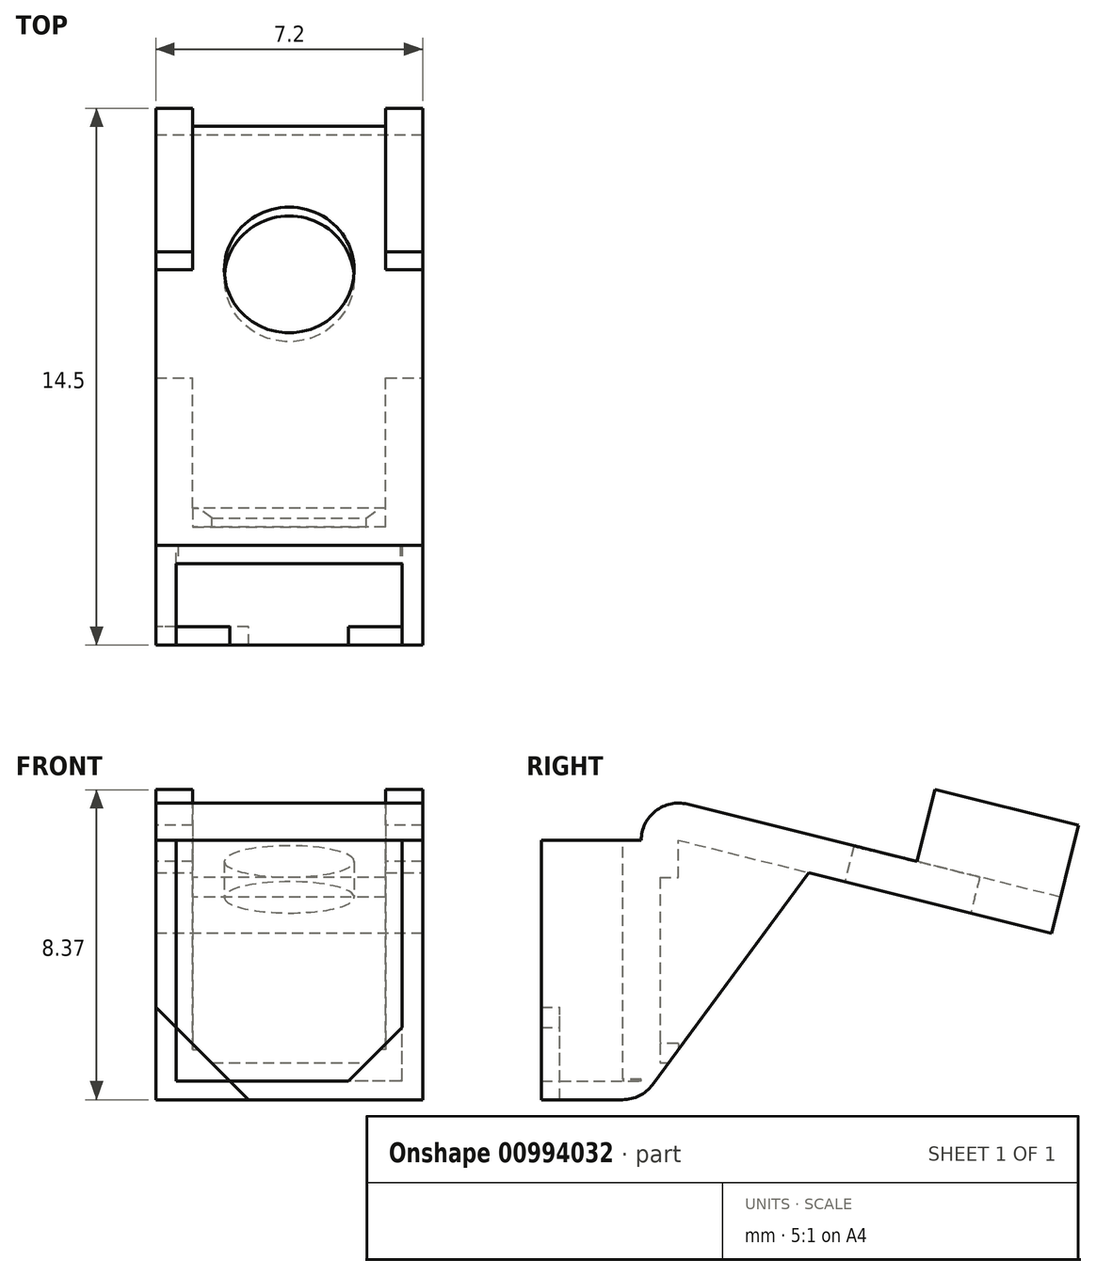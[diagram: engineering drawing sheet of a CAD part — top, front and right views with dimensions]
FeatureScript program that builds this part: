
annotation { "Feature Type Name" : "Feature", "Feature Type Description" : "" }
export const myFeature = defineFeature(function(context is Context, id is Id, definition is map)
    precondition{}
    {
        {
            var Q0;
            Q0=qCreatedBy(makeId("Front.planeOp"),FACE);
            var sketch = newSketch(context, id + "F0", { "sketchPlane" : qUnion([Q0])});
            skLineSegment(sketch, "E0.bottom", {"start": v(3.6, -3.5) * mm, "end": v(-3.6, -3.5) * mm});
            skLineSegment(sketch, "E0.top", {"start": v(3.6, 3.5) * mm, "end": v(-3.6, 3.5) * mm});
            skLineSegment(sketch, "E0.left", {"start": v(3.6, -3.5) * mm, "end": v(3.6, 3.5) * mm});
            skLineSegment(sketch, "E0.right", {"start": v(-3.6, -3.5) * mm, "end": v(-3.6, 3.5) * mm});
            skPoint(sketch, "E0.middle", {"position": v(0, 0) * mm});
            skLineSegment(sketch, "E1.bottom", {"start": v(3.05, -3) * mm, "end": v(-3.05, -3) * mm});
            skLineSegment(sketch, "E1.top", {"start": v(3.05, 3) * mm, "end": v(-3.05, 3) * mm});
            skLineSegment(sketch, "E1.left", {"start": v(3.05, -3) * mm, "end": v(3.05, 3) * mm});
            skLineSegment(sketch, "E1.right", {"start": v(-3.05, -3) * mm, "end": v(-3.05, 3) * mm});
            skLineSegment(sketch, "E2", {"start": v(-3.6, 3.5) * mm, "end": v(-3.6, 2.4) * mm});
            skLineSegment(sketch, "E3", {"start": v(-3.6, 3.5) * mm, "end": v(-2.5, 3.5) * mm});
            skLineSegment(sketch, "E4.MirrorCS", {"start": v(3.6, 3.5) * mm, "end": v(2.5, 3.5) * mm});
            skLineSegment(sketch, "E5.MirrorCS", {"start": v(3.6, 3.5) * mm, "end": v(3.6, 2.4) * mm});
            skLineSegment(sketch, "E6.MirrorCS", {"start": v(-3.6, -3.5) * mm, "end": v(-3.6, -2.4) * mm});
            skLineSegment(sketch, "E7.MirrorCS", {"start": v(-3.6, -3.5) * mm, "end": v(-2.5, -3.5) * mm});
            skLineSegment(sketch, "E8.MirrorCS", {"start": v(-3.05, -2.95) * mm, "end": v(-3, -3) * mm});
            skLineSegment(sketch, "E9.MirrorCS", {"start": v(3.6, -3.5) * mm, "end": v(2.5, -3.5) * mm});
            skLineSegment(sketch, "E10.MirrorCS", {"start": v(3.6, -3.5) * mm, "end": v(3.6, -2.4) * mm});
            skLineSegment(sketch, "E11.MirrorCS", {"start": v(3.05, -2.95) * mm, "end": v(3, -3) * mm});
            skPoint(sketch, "E12.orphan", {"position": v(-3.6, -2.4) * mm});
            skPoint(sketch, "E13.orphan", {"position": v(-2.5, -3.5) * mm});
            skPoint(sketch, "E14.orphan", {"position": v(2.5, -3.5) * mm});
            skPoint(sketch, "E15.orphan", {"position": v(3.6, -2.4) * mm});
            skPoint(sketch, "E16.orphan", {"position": v(2.5, 3.5) * mm});
            skPoint(sketch, "E17.orphan", {"position": v(3.6, 2.4) * mm});
            skLineSegment(sketch, "E18", {"start": v(-3.05, -3) * mm, "end": v(-3.05, -3.5) * mm});
            skLineSegment(sketch, "E19", {"start": v(3.05, -3) * mm, "end": v(3.05, -3.5) * mm});
            skLineSegment(sketch, "E20.MirrorCS", {"start": v(-3.05, 3) * mm, "end": v(-3.05, 3.5) * mm});
            skLineSegment(sketch, "E21.MirrorCS", {"start": v(3.05, 3) * mm, "end": v(3.05, 3.5) * mm});
            skSolve(sketch);
        }
        {
            var Q0;
            Q0=makeQuery(id+"F0.imprint","IMPRINT",FACE,{"disambiguationData":[TD([[makeQuery(id+"F0.imprint","IMPRINT",EDGE,{"derivedFrom":sQuery(id+"F0.wireOp",EDGE,"E0.right")}),-1.0]])]});
            var Q1;
            {var subQ5=sQuery(id+"F0.wireOp",EDGE,"E0.bottom");Q1=makeQuery(id+"F0.imprint","IMPRINT",FACE,{"disambiguationData":[TD([[makeQuery(id+"F0.imprint","IMPRINT",EDGE,{"derivedFrom":subQ5}),-1.0]])]});}
            var Q2;
            Q2=makeQuery(id+"F0.imprint","IMPRINT",FACE,{"disambiguationData":[TD([[makeQuery(id+"F0.imprint","IMPRINT",EDGE,{"derivedFrom":sQuery(id+"F0.wireOp",EDGE,"E0.left")}),1.0]])]});
            extrude(context, id + "F1", {"entities" : qUnion([Q0, Q1, Q2]), "depth" : 1.7 * mm, "offsetDistance" : 25 * mm});
        }
        {
            var Q0;
            Q0=makeQuery(id+"F0.imprint","IMPRINT",FACE,{"disambiguationData":[TD([[makeQuery(id+"F0.imprint","IMPRINT",EDGE,{"derivedFrom":sQuery(id+"F0.wireOp",EDGE,"E0.left")}),1.0]])]});
            var Q1;
            {var subQ5=sQuery(id+"F0.wireOp",EDGE,"E0.bottom");Q1=makeQuery(id+"F0.imprint","IMPRINT",FACE,{"disambiguationData":[TD([[makeQuery(id+"F0.imprint","IMPRINT",EDGE,{"derivedFrom":subQ5}),-1.0]])]});}
            var Q2;
            Q2=makeQuery(id+"F0.imprint","IMPRINT",FACE,{"disambiguationData":[TD([[makeQuery(id+"F0.imprint","IMPRINT",EDGE,{"derivedFrom":sQuery(id+"F0.wireOp",EDGE,"E0.right")}),-1.0]])]});
            var Q3;
            {var subQ1=sQuery(id+"F0.wireOp",EDGE,"E0.top");Q3=makeQuery(id+"F0.imprint","IMPRINT",FACE,{"disambiguationData":[TD([[makeQuery(id+"F0.imprint","IMPRINT",EDGE,{"derivedFrom":subQ1}),1.0]])]});}
            var Q4;
            {var subQ1=sQuery(id+"F0.wireOp",EDGE,"E1.top");Q4=makeQuery(id+"F0.imprint","IMPRINT",FACE,{"disambiguationData":[TD([[makeQuery(id+"F0.imprint","IMPRINT",EDGE,{"derivedFrom":subQ1}),1.0]])]});}
            extrude(context, id + "F2", {"entities" : qUnion([Q0, Q1, Q2, Q3, Q4]), "operationType" : NewBodyOperationType.ADD, "oppositeDirection" : true, "depth" : 0.5 * mm, "offsetDistance" : 25 * mm});
        }
        {
            var Q0;
            Q0=makeQuery(id+"F1.opExtrude","CAP_FACE",FACE,{"disambiguationData":[OSD([sQuery(id+"F0.wireOp",EDGE,"E0.bottom"),sQuery(id+"F0.wireOp",EDGE,"E0.top"),sQuery(id+"F0.wireOp",EDGE,"E0.left"),sQuery(id+"F0.wireOp",EDGE,"E0.right"),sQuery(id+"F0.wireOp",EDGE,"E1.bottom"),sQuery(id+"F0.wireOp",EDGE,"E1.top"),sQuery(id+"F0.wireOp",EDGE,"E1.left"),sQuery(id+"F0.wireOp",EDGE,"E1.right"),sQuery(id+"F0.wireOp",EDGE,"E2"),sQuery(id+"F0.wireOp",EDGE,"E3"),sQuery(id+"F0.wireOp",EDGE,"E4.MirrorCS"),sQuery(id+"F0.wireOp",EDGE,"E5.MirrorCS"),sQuery(id+"F0.wireOp",EDGE,"E6.MirrorCS"),sQuery(id+"F0.wireOp",EDGE,"E7.MirrorCS"),sQuery(id+"F0.wireOp",EDGE,"E9.MirrorCS"),sQuery(id+"F0.wireOp",EDGE,"E10.MirrorCS")])],"isStart":false});
            var sketch = newSketch(context, id + "F3", { "sketchPlane" : qUnion([Q0])});
            skLineSegment(sketch, "E22", {"start": v(-3.6, 3.5) * mm, "end": v(-1.1, 3.5) * mm});
            skLineSegment(sketch, "E23", {"start": v(-1.1, 3.5) * mm, "end": v(-3.6, 1) * mm});
            skLineSegment(sketch, "E24", {"start": v(-3.6, 1) * mm, "end": v(-3.6, 3.5) * mm});
            skLineSegment(sketch, "E25.MirrorCS", {"start": v(1.1, 3.5) * mm, "end": v(3.6, 1) * mm});
            skLineSegment(sketch, "E26.MirrorCS", {"start": v(3.6, 3.5) * mm, "end": v(1.1, 3.5) * mm});
            skLineSegment(sketch, "E27.MirrorCS", {"start": v(3.6, 1) * mm, "end": v(3.6, 3.5) * mm});
            skLineSegment(sketch, "E28.MirrorCS", {"start": v(-3.6, -3.5) * mm, "end": v(-1.1, -3.5) * mm});
            skLineSegment(sketch, "E29.MirrorCS", {"start": v(-3.6, -1) * mm, "end": v(-3.6, -3.5) * mm});
            skLineSegment(sketch, "E30.MirrorCS", {"start": v(-1.1, -3.5) * mm, "end": v(-3.6, -1) * mm});
            skLineSegment(sketch, "E31.MirrorCS", {"start": v(3.6, -3.5) * mm, "end": v(1.1, -3.5) * mm});
            skLineSegment(sketch, "E32.MirrorCS", {"start": v(3.6, -1) * mm, "end": v(3.6, -3.5) * mm});
            skLineSegment(sketch, "E33.MirrorCS", {"start": v(1.1, -3.5) * mm, "end": v(3.6, -1) * mm});
            skSolve(sketch);
        }
        {
            var Q0;
            {var subQ4=sQuery(id+"F3.wireOp",EDGE,"E22");Q0=makeQuery(id+"F3.imprint","IMPRINT",FACE,{"disambiguationData":[TD([[makeQuery(id+"F3.imprint","IMPRINT",EDGE,{"derivedFrom":subQ4}),1.0]])]});}
            var Q1;
            {var subQ0=sQuery(id+"F3.wireOp",EDGE,"E29.MirrorCS");Q1=makeQuery(id+"F3.imprint","IMPRINT",FACE,{"disambiguationData":[TD([[makeQuery(id+"F3.imprint","IMPRINT",EDGE,{"derivedFrom":subQ0}),1.0]])]});}
            var Q2;
            {var subQ0=sQuery(id+"F3.wireOp",EDGE,"E23");var subQ3=makeQuery(id+"F1.opExtrude","CAP_EDGE",EDGE,{"disambiguationData":[OSD([sQuery(id+"F0.wireOp",EDGE,"E1.top")])],"isStart":false});var subQ4=makeQuery(id+"F3.imprint","INTERSECT",VERTEX,{"derivedFrom":[subQ3,subQ0]});Q2=makeQuery(id+"F3.imprint","IMPRINT",FACE,{"disambiguationData":[TD([[makeQuery(id+"F3.imprint","IMPRINT",EDGE,{"disambiguationData":[TD([[subQ4,1.0]])],"derivedFrom":subQ3}),-1.0]])]});}
            var Q3;
            {var subQ0=sQuery(id+"F3.wireOp",EDGE,"E25.MirrorCS");var subQ3=makeQuery(id+"F1.opExtrude","CAP_EDGE",EDGE,{"disambiguationData":[OSD([sQuery(id+"F0.wireOp",EDGE,"E1.left"),sQuery(id+"F0.wireOp",EDGE,"E19")])],"isStart":false});var subQ4=makeQuery(id+"F3.imprint","INTERSECT",VERTEX,{"derivedFrom":[subQ3,subQ0]});Q3=makeQuery(id+"F3.imprint","IMPRINT",FACE,{"disambiguationData":[TD([[makeQuery(id+"F3.imprint","IMPRINT",EDGE,{"disambiguationData":[TD([[subQ4,1.0]])],"derivedFrom":subQ3}),-1.0]])]});}
            var Q4;
            {var subQ0=sQuery(id+"F3.wireOp",EDGE,"E32.MirrorCS");Q4=makeQuery(id+"F3.imprint","IMPRINT",FACE,{"disambiguationData":[TD([[makeQuery(id+"F3.imprint","IMPRINT",EDGE,{"derivedFrom":subQ0}),1.0]])]});}
            var Q5;
            {var subQ0=sQuery(id+"F3.wireOp",EDGE,"E24");Q5=makeQuery(id+"F3.imprint","IMPRINT",FACE,{"disambiguationData":[TD([[makeQuery(id+"F3.imprint","IMPRINT",EDGE,{"derivedFrom":subQ0}),1.0]])]});}
            var Q6;
            {var subQ0=sQuery(id+"F3.wireOp",EDGE,"E23");var subQ3=makeQuery(id+"F1.opExtrude","CAP_EDGE",EDGE,{"disambiguationData":[OSD([sQuery(id+"F0.wireOp",EDGE,"E1.right"),sQuery(id+"F0.wireOp",EDGE,"E20.MirrorCS")])],"isStart":false});var subQ4=makeQuery(id+"F3.imprint","INTERSECT",VERTEX,{"derivedFrom":[subQ3,subQ0]});Q6=makeQuery(id+"F3.imprint","IMPRINT",FACE,{"disambiguationData":[TD([[makeQuery(id+"F3.imprint","IMPRINT",EDGE,{"disambiguationData":[TD([[subQ4,1.0]])],"derivedFrom":subQ3}),1.0]])]});}
            var Q7;
            {var subQ0=sQuery(id+"F3.wireOp",EDGE,"E27.MirrorCS");Q7=makeQuery(id+"F3.imprint","IMPRINT",FACE,{"disambiguationData":[TD([[makeQuery(id+"F3.imprint","IMPRINT",EDGE,{"derivedFrom":subQ0}),1.0]])]});}
            var Q8;
            {var subQ0=sQuery(id+"F3.wireOp",EDGE,"E30.MirrorCS");var subQ3=makeQuery(id+"F1.opExtrude","CAP_EDGE",EDGE,{"disambiguationData":[OSD([sQuery(id+"F0.wireOp",EDGE,"E1.bottom")])],"isStart":false});var subQ4=makeQuery(id+"F3.imprint","INTERSECT",VERTEX,{"derivedFrom":[subQ3,subQ0]});Q8=makeQuery(id+"F3.imprint","IMPRINT",FACE,{"disambiguationData":[TD([[makeQuery(id+"F3.imprint","IMPRINT",EDGE,{"disambiguationData":[TD([[subQ4,1.0]])],"derivedFrom":subQ3}),1.0]])]});}
            var Q9;
            {var subQ0=sQuery(id+"F3.wireOp",EDGE,"E33.MirrorCS");var subQ1=makeQuery(id+"F1.opExtrude","CAP_EDGE",EDGE,{"disambiguationData":[OSD([sQuery(id+"F0.wireOp",EDGE,"E1.bottom")])],"isStart":false});var subQ2=makeQuery(id+"F3.imprint","INTERSECT",VERTEX,{"derivedFrom":[subQ1,subQ0]});Q9=makeQuery(id+"F3.imprint","IMPRINT",FACE,{"disambiguationData":[TD([[makeQuery(id+"F3.imprint","IMPRINT",EDGE,{"disambiguationData":[TD([[subQ2,-1.0]])],"derivedFrom":subQ0}),-1.0]])]});}
            var Q10;
            {var subQ0=sQuery(id+"F3.wireOp",EDGE,"E30.MirrorCS");var subQ1=makeQuery(id+"F1.opExtrude","CAP_EDGE",EDGE,{"disambiguationData":[OSD([sQuery(id+"F0.wireOp",EDGE,"E1.bottom")])],"isStart":false});var subQ2=makeQuery(id+"F3.imprint","INTERSECT",VERTEX,{"derivedFrom":[subQ1,subQ0]});Q10=makeQuery(id+"F3.imprint","IMPRINT",FACE,{"disambiguationData":[TD([[makeQuery(id+"F3.imprint","IMPRINT",EDGE,{"disambiguationData":[TD([[subQ2,-1.0]])],"derivedFrom":subQ0}),1.0]])]});}
            extrude(context, id + "F4", {"entities" : qUnion([Q0, Q1, Q2, Q3, Q4, Q5, Q6, Q7, Q8, Q9, Q10]), "operationType" : NewBodyOperationType.ADD, "depth" : 0.5 * mm, "offsetDistance" : 25 * mm});
        }
        {
            var Q0;
            {var subQ0=sQuery(id+"F0.wireOp",EDGE,"E10.MirrorCS");var subQ1=sQuery(id+"F0.wireOp",EDGE,"E5.MirrorCS");var subQ2=sQuery(id+"F0.wireOp",EDGE,"E0.left");Q0=makeQuery(id+"F4.boolean.opBoolean","MERGE",FACE,{"derivedFrom":[makeQuery(id+"F2.boolean.opBoolean","MERGE",FACE,{"derivedFrom":[makeQuery(id+"F1.opExtrude","SWEPT_FACE",FACE,{"disambiguationData":[OSD([subQ2,subQ1,subQ0])]}),makeQuery(id+"F2.opExtrude","SWEPT_FACE",FACE,{"disambiguationData":[OSD([subQ2,subQ1,subQ0])]})]}),makeQuery(id+"F4.opExtrude","SWEPT_FACE",FACE,{"disambiguationData":[OSD([subQ2,subQ1,subQ0,sQuery(id+"F3.wireOp",EDGE,"E27.MirrorCS"),sQuery(id+"F3.wireOp",EDGE,"E32.MirrorCS")])]})]});}
            var sketch = newSketch(context, id + "F5", { "sketchPlane" : qUnion([Q0])});
            skLineSegment(sketch, "E34", {"start": v(0.5, -3.5) * mm, "end": v(5.66, 3.5) * mm});
            skLineSegment(sketch, "E35", {"start": v(5.66, 3.5) * mm, "end": v(0.5, 3.5) * mm});
            skLineSegment(sketch, "E36", {"start": v(0.5, 3.5) * mm, "end": v(0.5, 4.79) * mm});
            skLineSegment(sketch, "E37", {"start": v(0.5, 4.79) * mm, "end": v(5.66, 3.5) * mm});
            skSolve(sketch);
        }
        {
            var Q0;
            Q0=makeQuery(id+"F5.imprint","IMPRINT",FACE,{"disambiguationData":[TD([[makeQuery(id+"F5.imprint","IMPRINT",EDGE,{"derivedFrom":sQuery(id+"F5.wireOp",EDGE,"E34")}),1.0]])]});
            var Q1;
            Q1=makeQuery(id+"F5.imprint","IMPRINT",FACE,{"disambiguationData":[TD([[makeQuery(id+"F5.imprint","IMPRINT",EDGE,{"derivedFrom":sQuery(id+"F5.wireOp",EDGE,"E35")}),-1.0]])]});
            extrude(context, id + "F6", {"entities" : qUnion([Q0, Q1]), "operationType" : NewBodyOperationType.ADD, "oppositeDirection" : true, "depth" : 7.2 * mm, "offsetDistance" : 25 * mm});
        }
        {
            var Q0;
            Q0=makeQuery(id+"F6.opExtrude","SWEPT_FACE",FACE,{"disambiguationData":[OSD([sQuery(id+"F5.wireOp",EDGE,"E37")])]});
            var sketch = newSketch(context, id + "F7", { "sketchPlane" : qUnion([Q0])});
            skLineSegment(sketch, "E38.bottom", {"start": v(3.6, 1.99) * mm, "end": v(-3.6, 1.99) * mm});
            skLineSegment(sketch, "E38.top", {"start": v(3.6, 10.99) * mm, "end": v(-3.6, 10.99) * mm});
            skLineSegment(sketch, "E38.left", {"start": v(3.6, 1.99) * mm, "end": v(3.6, 10.99) * mm});
            skLineSegment(sketch, "E38.right", {"start": v(-3.6, 1.99) * mm, "end": v(-3.6, 10.99) * mm});
            skSolve(sketch);
        }
        {
            var Q0;
            {var subQ0=sQuery(id+"F7.wireOp",EDGE,"E38.bottom");Q0=makeQuery(id+"F7.imprint","IMPRINT",FACE,{"disambiguationData":[TD([[makeQuery(id+"F7.imprint","IMPRINT",EDGE,{"derivedFrom":subQ0}),-1.0]])]});}
            var Q1;
            {var subQ0=sQuery(id+"F7.wireOp",EDGE,"E38.top");Q1=makeQuery(id+"F7.imprint","IMPRINT",FACE,{"disambiguationData":[TD([[makeQuery(id+"F7.imprint","IMPRINT",EDGE,{"derivedFrom":subQ0}),1.0]])]});}
            extrude(context, id + "F8", {"entities" : qUnion([Q0, Q1]), "operationType" : NewBodyOperationType.ADD, "oppositeDirection" : true, "depth" : 1 * mm, "offsetDistance" : 25 * mm});
        }
        {
            var Q0;
            Q0=makeQuery(id+"F6.opExtrude","SWEPT_EDGE",EDGE,{"disambiguationData":[OSD([sQuery(id+"F5.wireOp",EDGE,"E36"),sQuery(id+"F5.wireOp",EDGE,"E37")])]});
            var Q1;
            {var subQ0=sQuery(id+"F0.wireOp",EDGE,"E9.MirrorCS");Q1=makeQuery(id+"F6.boolean.opBoolean","MERGE",EDGE,{"derivedFrom":[makeQuery(id+"F2.opExtrude","CAP_EDGE",EDGE,{"disambiguationData":[OSD([sQuery(id+"F0.wireOp",EDGE,"E0.bottom"),sQuery(id+"F0.wireOp",EDGE,"E7.MirrorCS"),subQ0])],"isStart":false}),makeQuery(id+"F6.opExtrude","SWEPT_EDGE",EDGE,{"disambiguationData":[OSD([sQuery(id+"F0.wireOp",EDGE,"E0.left"),sQuery(id+"F0.wireOp",EDGE,"E5.MirrorCS"),subQ0,sQuery(id+"F0.wireOp",EDGE,"E10.MirrorCS"),sQuery(id+"F3.wireOp",EDGE,"E31.MirrorCS"),sQuery(id+"F3.wireOp",EDGE,"E32.MirrorCS"),sQuery(id+"F5.wireOp",EDGE,"E34")])]})]});}
            fillet(context, id + "F9", {"entities" : qUnion([Q0, Q1]), "radius" : 1 * mm, "tangentPropagation" : true, "allowEdgeOverflow" : false});
        }
        {
            var Q0;
            Q0=makeQuery(id+"F6.opExtrude","SWEPT_FACE",FACE,{"disambiguationData":[OSD([sQuery(id+"F5.wireOp",EDGE,"E34")])]});
            var Q1;
            Q1=makeQuery(id+"Fk9uV9KjEYSot8e_1.opExtrude","SWEPT_FACE",FACE,{"disambiguationData":[OSD([sQuery(id+"F63APWi9Rhe5ELq_1.wireOp",EDGE,"XRLtQqb1-nqzG-HNpP-SYgB-2mY2Ma2ogBY2")])]});
            var Q2;
            Q2=makeQuery(id+"Fk9uV9KjEYSot8e_1.opExtrude","SWEPT_FACE",FACE,{"disambiguationData":[OSD([sQuery(id+"F63APWi9Rhe5ELq_1.wireOp",EDGE,"cmMQ0UmM-WrUb-k1j2-ASJz-lQ1dVbu4DDY7")])]});
            shell(context, id + "F10", {"entities" : qUnion([Q0, Q1, Q2]), "thickness" : 1 * mm});
        }
        {
            var Q0;
            Q0=makeQuery(id+"F10.opShell","OFFSET_FACE",FACE,{"disambiguationData":[OSD([sQuery(id+"F5.wireOp",EDGE,"E37"),sQuery(id+"F7.wireOp",EDGE,"E38.bottom"),sQuery(id+"F7.wireOp",EDGE,"E38.top"),sQuery(id+"F7.wireOp",EDGE,"E38.left"),sQuery(id+"F7.wireOp",EDGE,"E38.right")])]});
            var sketch = newSketch(context, id + "F11", { "sketchPlane" : qUnion([Q0])});
            skCircle(sketch, "E39", {"center": v(0, -6.99) * mm, "radius": 1.75 * mm});
            skSolve(sketch);
        }
        {
            var Q0;
            Q0=makeQuery(id+"F11.imprint","IMPRINT",FACE,{"disambiguationData":[TD([[makeQuery(id+"F11.imprint","IMPRINT",EDGE,{"derivedFrom":sQuery(id+"F11.wireOp",EDGE,"E39")}),1.0]])]});
            extrude(context, id + "F12", {"entities" : qUnion([Q0]), "operationType" : NewBodyOperationType.REMOVE, "oppositeDirection" : true, "depth" : 2 * mm, "offsetDistance" : 25 * mm});
        }
        {
            var Q0;
            Q0=makeQuery(id+"F8.boolean.opBoolean","MERGE",FACE,{"derivedFrom":[makeQuery(id+"F6.opExtrude","SWEPT_FACE",FACE,{"disambiguationData":[OSD([sQuery(id+"F5.wireOp",EDGE,"E37")])]}),makeQuery(id+"F8.opExtrude","CAP_FACE",FACE,{"disambiguationData":[OSD([sQuery(id+"F7.wireOp",EDGE,"E38.bottom"),sQuery(id+"F7.wireOp",EDGE,"E38.top"),sQuery(id+"F7.wireOp",EDGE,"E38.left"),sQuery(id+"F7.wireOp",EDGE,"E38.right")])],"isStart":true})]});
            var sketch = newSketch(context, id + "F13", { "sketchPlane" : qUnion([Q0])});
            skLineSegment(sketch, "E40.bottom", {"start": v(3.6, 10.99) * mm, "end": v(-3.6, 10.99) * mm});
            skLineSegment(sketch, "E40.top", {"start": v(3.6, 7) * mm, "end": v(-3.6, 7) * mm});
            skLineSegment(sketch, "E40.left", {"start": v(3.6, 10.99) * mm, "end": v(3.6, 7) * mm});
            skLineSegment(sketch, "E40.right", {"start": v(-3.6, 10.99) * mm, "end": v(-3.6, 7) * mm});
            skLineSegment(sketch, "E41", {"start": v(2.6, 10.99) * mm, "end": v(2.6, 7) * mm});
            skLineSegment(sketch, "E42.MirrorCS", {"start": v(-2.6, 10.99) * mm, "end": v(-2.6, 7) * mm});
            skSolve(sketch);
        }
        {
            var Q0;
            Q0=makeQuery(id+"F13.imprint","IMPRINT",FACE,{"disambiguationData":[TD([[makeQuery(id+"F13.imprint","IMPRINT",EDGE,{"derivedFrom":sQuery(id+"F13.wireOp",EDGE,"E40.bottom")}),1.0]])]});
            extrude(context, id + "F14", {"entities" : qUnion([Q0]), "operationType" : NewBodyOperationType.ADD, "depth" : 2 * mm, "offsetDistance" : 25 * mm});
        }
    });
